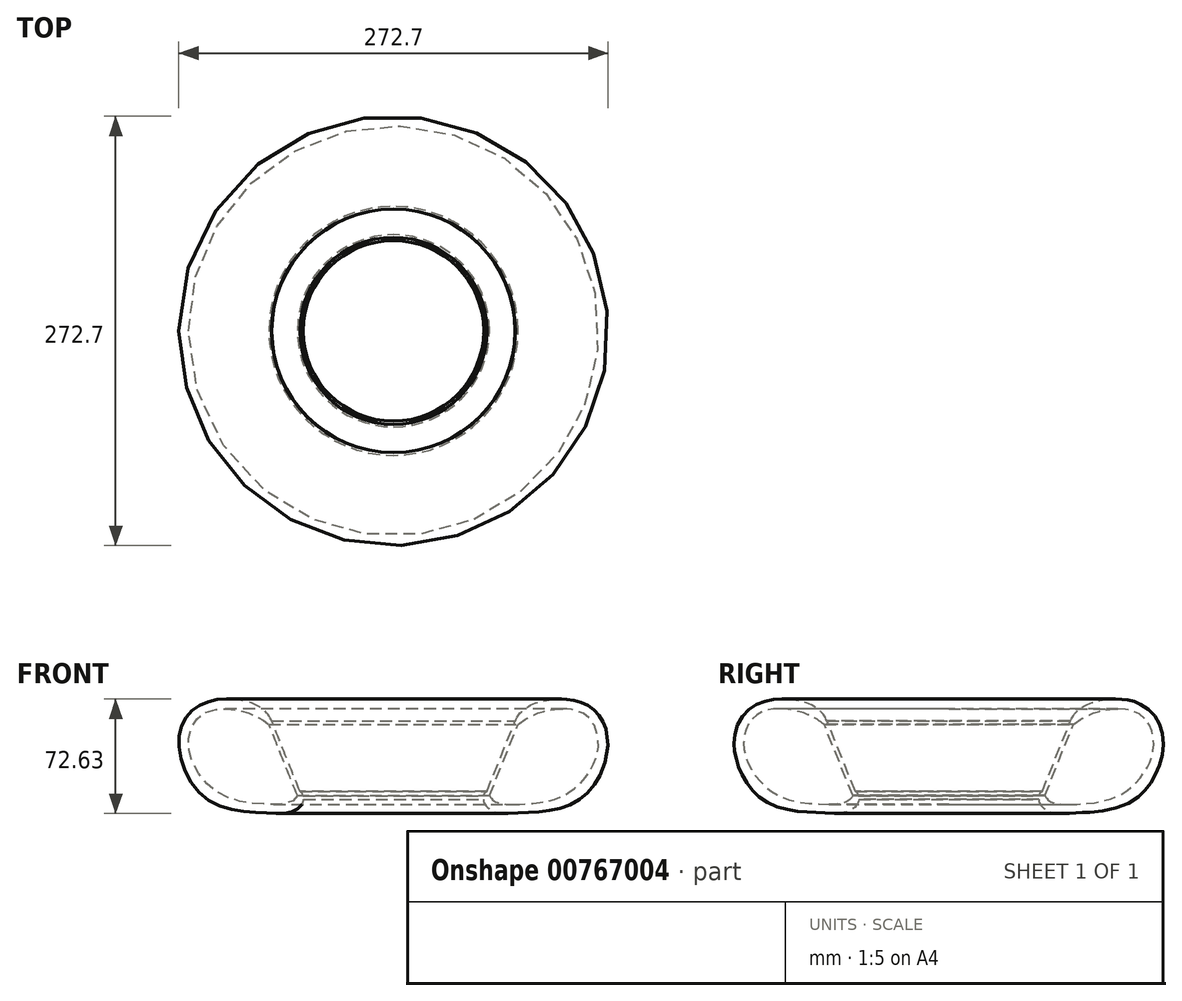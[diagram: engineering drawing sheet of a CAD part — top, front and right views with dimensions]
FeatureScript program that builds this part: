
annotation { "Feature Type Name" : "Feature", "Feature Type Description" : "" }
export const myFeature = defineFeature(function(context is Context, id is Id, definition is map)
    precondition{}
    {
        {
            var Q0;
            Q0=qCreatedBy(makeId("Front.planeOp"),FACE);
            var sketch = newSketch(context, id + "F0", { "sketchPlane" : qUnion([Q0])});
            skLineSegment(sketch, "E0.MirrorCS", {"start": v(-79.78, 49.54) * mm, "end": v(0.22, 49.54) * mm});
            skLineSegment(sketch, "E1", {"start": v(-79.78, 49.54) * mm, "end": v(-59.78, -0.46) * mm});
            skLineSegment(sketch, "E2", {"start": v(0.22, 49.54) * mm, "end": v(0.22, -0.46) * mm});
            skLineSegment(sketch, "E3", {"start": v(-59.78, -0.46) * mm, "end": v(0.22, -0.46) * mm});
            skSolve(sketch);
        }
        {
            var Q0;
            Q0=qCreatedBy(makeId("Front.planeOp"),FACE);
            var sketch = newSketch(context, id + "F1", { "sketchPlane" : qUnion([Q0])});
            skFitSpline(sketch, "E4.MirrorC", {"points": [v(-80.8, 55.17) * mm, v(-103.42, 63.39) * mm, v(-125.8, 57.52) * mm, v(-136.14, 35.5) * mm, v(-118.2, -0.22) * mm, v(-80.97, -8.9) * mm, v(-62.78, -7.62) * mm, v(-56.86, -0.22) * mm, v(-58.98, 4.64) * mm, v(-62.36, -0.22) * mm, v(-81.4, -3.4) * mm, v(-112.27, 4.64) * mm, v(-129.94, 33.35) * mm, v(-119.79, 54.52) * mm, v(-93.94, 55.23) * mm, v(-80.53, 48.45) * mm, v(-76.75, 46.54) * mm, v(-80.8, 55.17) * mm]});
            skSolve(sketch);
        }
        {
            var Q0;
            Q0=makeQuery(id+"F0.imprint","IMPRINT",FACE,{"disambiguationData":[TD([[makeQuery(id+"F0.imprint","IMPRINT",EDGE,{"derivedFrom":sQuery(id+"F0.wireOp",EDGE,"E0.MirrorCS")}),-1.0]])]});
            var Q1;
            Q1=sQuery(id+"F0.wireOp",EDGE,"E2");
            revolve(context, id + "F2", {"surfaceOperationType" : NewSurfaceOperationType.NEW, "entities" : qUnion([Q0]), "axis" : qUnion([Q1]), "revolveType" : RevolveType.FULL});
        }
        {
            var Q0;
            Q0=makeQuery(id+"F2.opRevolve","SWEPT_FACE",FACE,{"disambiguationData":[OSD([sQuery(id+"F0.wireOp",EDGE,"E0.MirrorCS")])]});
            shell(context, id + "F3", {"entities" : qUnion([Q0]), "thickness" : 2.5 * mm});
        }
        {
            var Q0;
            Q0=makeQuery(id+"F1.imprint","IMPRINT",FACE,{"disambiguationData":[TD([[makeQuery(id+"F1.imprint","IMPRINT",EDGE,{"derivedFrom":sQuery(id+"F1.wireOp",EDGE,"E4.MirrorC")}),1.0]])]});
            var Q1;
            Q1=makeQuery(id+"F2.opRevolve","SWEPT_FACE",FACE,{"disambiguationData":[OSD([sQuery(id+"F0.wireOp",EDGE,"E1")])]});
            revolve(context, id + "F4", {"operationType" : NewBodyOperationType.ADD, "surfaceOperationType" : NewSurfaceOperationType.NEW, "entities" : qUnion([Q0]), "axis" : qUnion([Q1]), "revolveType" : RevolveType.FULL});
        }
    });
